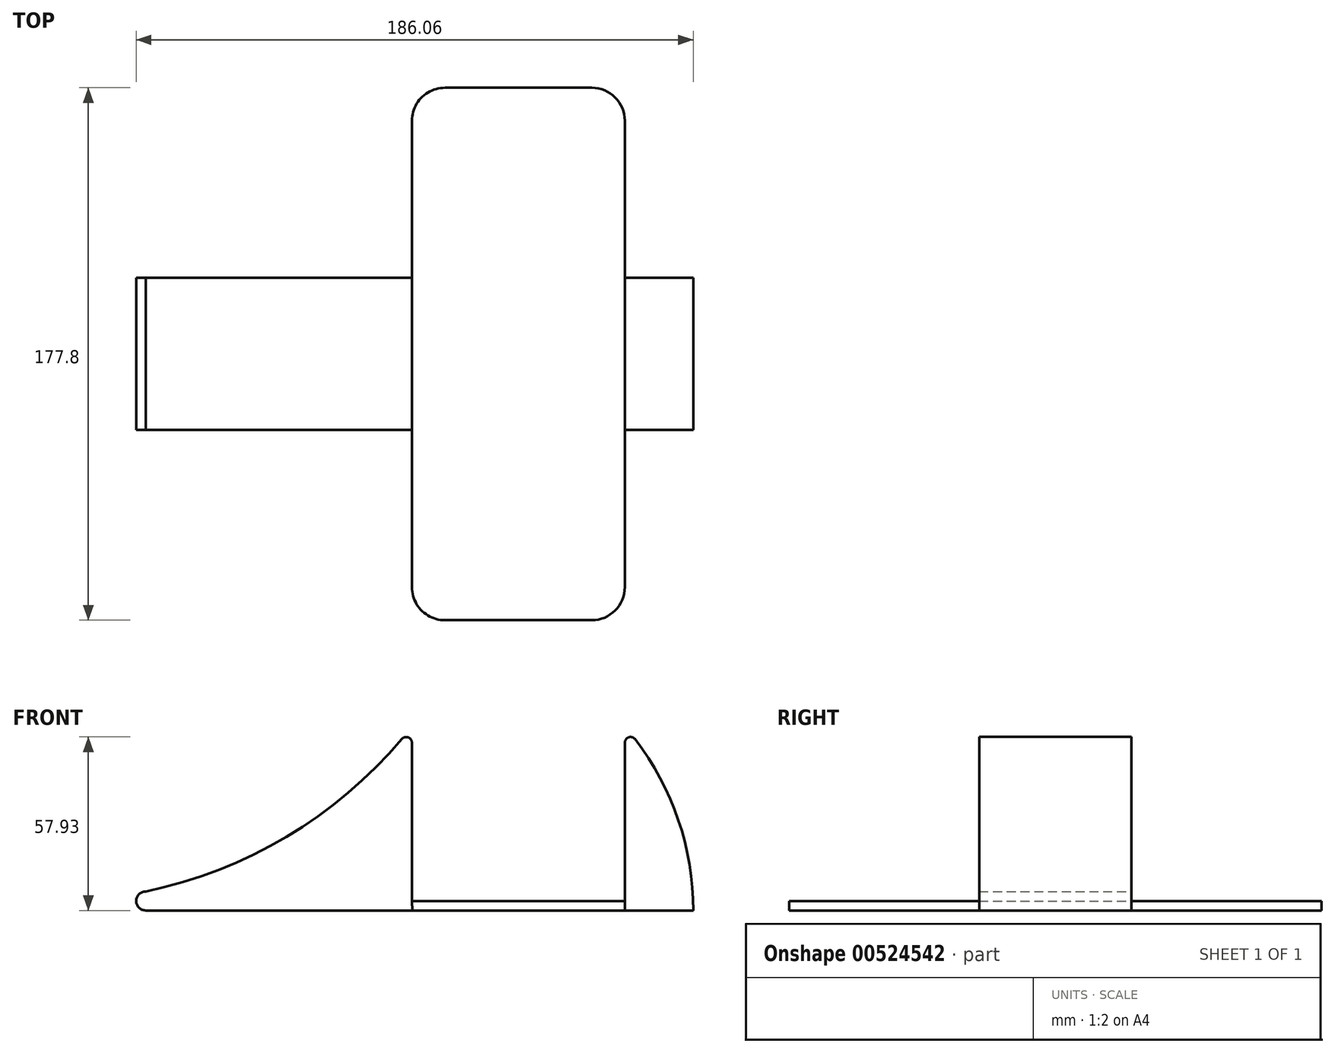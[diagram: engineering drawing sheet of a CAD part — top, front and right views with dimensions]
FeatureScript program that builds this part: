
annotation { "Feature Type Name" : "Feature", "Feature Type Description" : "" }
export const myFeature = defineFeature(function(context is Context, id is Id, definition is map)
    precondition{}
    {
        {
            var Q0;
            Q0=qCreatedBy(makeId("Front.planeOp"),FACE);
            var sketch = newSketch(context, id + "F0", { "sketchPlane" : qUnion([Q0])});
            skLineSegment(sketch, "E0.top", {"start": v(33.02, -30.69) * mm, "end": v(-33.02, -30.69) * mm});
            skPoint(sketch, "E0.middle", {"position": v(0, 0) * mm});
            skLineSegment(sketch, "E1", {"start": v(-33.02, -30.69) * mm, "end": v(-124.46, -30.69) * mm});
            skLineSegment(sketch, "E2.bottom", {"start": v(-124.46, -30.69) * mm, "end": v(-33.02, -30.69) * mm});
            skLineSegment(sketch, "E2.left", {"start": v(-124.46, -30.69) * mm, "end": v(-124.46, -24.34) * mm});
            skLineSegment(sketch, "E3", {"start": v(-35.56, 30.69) * mm, "end": v(-35.56, -24.34) * mm});
            skLineSegment(sketch, "E4.bottom", {"start": v(58.2, -24.34) * mm, "end": v(58.42, -24.34) * mm});
            skLineSegment(sketch, "E4.top", {"start": v(-33.02, -30.69) * mm, "end": v(58.42, -30.69) * mm});
            skLineSegment(sketch, "E4.right", {"start": v(58.42, -24.34) * mm, "end": v(58.42, -30.69) * mm});
            skLineSegment(sketch, "E5", {"start": v(35.56, 30.69) * mm, "end": v(35.56, -24.34) * mm});
            skLineSegment(sketch, "E6", {"start": v(58.16, -23.71) * mm, "end": v(58.42, -24.34) * mm});
            skLineSegment(sketch, "E7", {"start": v(-35.56, -24.34) * mm, "end": v(-35.56, -27.51) * mm});
            skLineSegment(sketch, "E8", {"start": v(35.56, -24.34) * mm, "end": v(35.56, -27.51) * mm});
            skLineSegment(sketch, "E9", {"start": v(-35.56, -27.51) * mm, "end": v(35.56, -27.51) * mm});
            skPoint(sketch, "E10.start.orphan", {"position": v(-33.02, 30.69) * mm});
            skPoint(sketch, "E11.orphan", {"position": v(33.02, 30.69) * mm});
            skArc(sketch, "E12", {"start": v(58.42, -30.69) * mm, "mid": v(52.52, 2.06) * mm, "end": v(35.56, 30.69) * mm});
            skArc(sketch, "E13", {"start": v(-124.46, -24.34) * mm, "mid": v(-75.13, -4.71) * mm, "end": v(-35.56, 30.69) * mm});
            skPoint(sketch, "E14.end.orphan", {"position": v(-78.74, -24.34) * mm});
            skPoint(sketch, "E15.orphan", {"position": v(-33.02, -24.34) * mm});
            skPoint(sketch, "E16.orphan", {"position": v(35.56, -30.69) * mm});
            skPoint(sketch, "E17.orphan", {"position": v(-35.56, -30.69) * mm});
            skArc(sketch, "E18", {"start": v(-124.46, -24.34) * mm, "mid": v(-127.64, -27.51) * mm, "end": v(-124.46, -30.69) * mm});
            skLineSegment(sketch, "E19", {"start": v(-35.4, -30.69) * mm, "end": v(-35.56, -27.51) * mm});
            skLineSegment(sketch, "E20", {"start": v(35.56, -30.69) * mm, "end": v(35.56, -27.51) * mm});
            skSolve(sketch);
        }
        {
            var Q0;
            Q0=makeQuery(id+"F0.imprint","IMPRINT",FACE,{"disambiguationData":[TD([[makeQuery(id+"F0.imprint","IMPRINT",EDGE,{"derivedFrom":sQuery(id+"F0.wireOp",EDGE,"E2.left")}),1.0]])]});
            var Q1;
            {var subQ0=sQuery(id+"F0.wireOp",EDGE,"E2.left");Q1=makeQuery(id+"F0.imprint","IMPRINT",FACE,{"disambiguationData":[TD([[makeQuery(id+"F0.imprint","IMPRINT",EDGE,{"derivedFrom":subQ0}),-1.0]])]});}
            var Q2;
            {var subQ4=sQuery(id+"F0.wireOp",EDGE,"E5");Q2=makeQuery(id+"F0.imprint","IMPRINT",FACE,{"disambiguationData":[TD([[makeQuery(id+"F0.imprint","IMPRINT",EDGE,{"derivedFrom":subQ4}),1.0]])]});}
            extrude(context, id + "F1", {"entities" : qUnion([Q0, Q1, Q2]), "depth" : 50.8 * mm, "offsetDistance" : 25.4 * mm});
        }
        {
            var Q0;
            Q0=makeQuery(id+"F0.imprint","IMPRINT",FACE,{"disambiguationData":[TD([[makeQuery(id+"F0.imprint","IMPRINT",EDGE,{"derivedFrom":sQuery(id+"F0.wireOp",EDGE,"E9")}),-1.0]])]});
            extrude(context, id + "F2", {"entities" : qUnion([Q0]), "depth" : 114.3 * mm, "offsetDistance" : 25.4 * mm});
        }
        {
            var Q0;
            Q0=makeQuery(id+"F0.imprint","IMPRINT",FACE,{"disambiguationData":[TD([[makeQuery(id+"F0.imprint","IMPRINT",EDGE,{"derivedFrom":sQuery(id+"F0.wireOp",EDGE,"E9")}),-1.0]])]});
            extrude(context, id + "F3", {"entities" : qUnion([Q0]), "operationType" : NewBodyOperationType.ADD, "oppositeDirection" : true, "depth" : 63.5 * mm, "offsetDistance" : 25.4 * mm});
        }
        {
            var Q0;
            Q0=makeQuery(id+"F1.opExtrude","SWEPT_EDGE",EDGE,{"disambiguationData":[OSD([sQuery(id+"F0.wireOp",EDGE,"E3"),sQuery(id+"F0.wireOp",EDGE,"E13")])]});
            var Q1;
            Q1=makeQuery(id+"F1.opExtrude","SWEPT_EDGE",EDGE,{"disambiguationData":[OSD([sQuery(id+"F0.wireOp",EDGE,"E5"),sQuery(id+"F0.wireOp",EDGE,"E12")])]});
            fillet(context, id + "F4", {"entities" : qUnion([Q0, Q1]), "radius" : 1.9 * mm, "tangentPropagation" : true, "allowEdgeOverflow" : false});
        }
        {
            var Q0;
            Q0=makeQuery(id+"F2.opExtrude","CAP_EDGE",EDGE,{"disambiguationData":[OSD([sQuery(id+"F0.wireOp",EDGE,"E19")])],"isStart":false});
            var Q1;
            Q1=makeQuery(id+"F2.opExtrude","CAP_EDGE",EDGE,{"disambiguationData":[OSD([sQuery(id+"F0.wireOp",EDGE,"E20")])],"isStart":false});
            var Q2;
            Q2=makeQuery(id+"F3.opExtrude","CAP_EDGE",EDGE,{"disambiguationData":[OSD([sQuery(id+"F0.wireOp",EDGE,"E20")])],"isStart":false});
            var Q3;
            Q3=makeQuery(id+"F3.opExtrude","CAP_EDGE",EDGE,{"disambiguationData":[OSD([sQuery(id+"F0.wireOp",EDGE,"E19")])],"isStart":false});
            fillet(context, id + "F5", {"entities" : qUnion([Q0, Q1, Q2, Q3]), "radius" : 11.04 * mm, "tangentPropagation" : true, "allowEdgeOverflow" : false});
        }
    });
